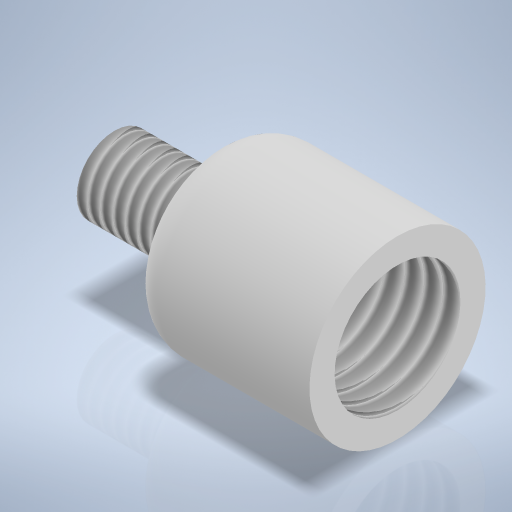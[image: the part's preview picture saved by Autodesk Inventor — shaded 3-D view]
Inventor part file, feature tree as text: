
AUTODESK INVENTOR PART (.ipt)
format: ipt  version: 2024 (Build 280153000, 153)  size: 314,880 bytes
history: native  units: mm
features: revolve x2, thread x2, sketch x2, fillet x1
ambient origin geometry x8: Origin, YZ Plane, XZ Plane, XY Plane, X Axis, Y Axis, Z Axis, Center Point
bodies: Volumenkörper1 (feature_tree)
feature tree (7):
  revolve  "Umdrehung1"
  thread  "Gewinde1"  [1 undecoded]
  revolve  "Umdrehung2"
  fillet  "Rundung1"  Radius=8.0mm
  thread  "Gewinde2"  [1 undecoded]
  sketch  "Skizze1"  dims[d3=14.0mm]
  sketch  "Skizze2"  dims[d4=2.5mm d5=90.0deg d6=8.0mm d7=0.0mm d8=3.0mm d9=9.5mm d12=10.0mm d13=11.5mm d14=90.0deg d15=2.0mm d16=10.181mm d17=0.0mm]
note: 2 required parameter values undecoded (feature->parameter linkage not recoverable at this tier; creation-order binding heuristic only, values carry confidence <= 0.55)
